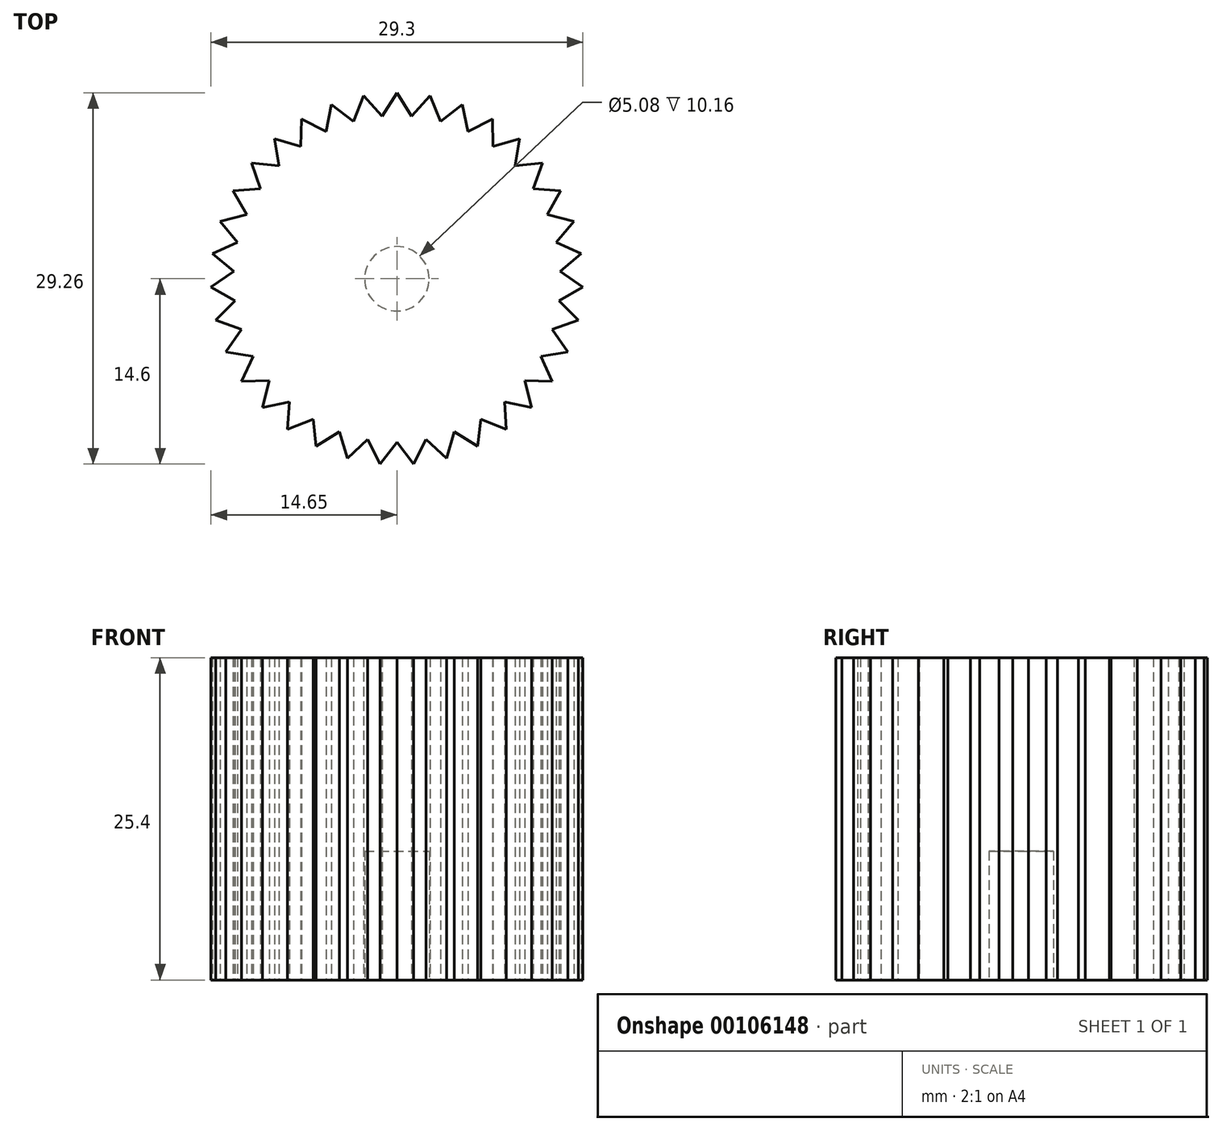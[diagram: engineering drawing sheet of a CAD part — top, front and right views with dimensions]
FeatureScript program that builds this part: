
annotation { "Feature Type Name" : "Feature", "Feature Type Description" : "" }
export const myFeature = defineFeature(function(context is Context, id is Id, definition is map)
    precondition{}
    {
        {
            var Q0;
            Q0=qCreatedBy(makeId("Top.planeOp"),FACE);
            var sketch = newSketch(context, id + "F0", { "sketchPlane" : qUnion([Q0])});
            skCircle(sketch, "E0", {"center": v(0, 0) * mm, "radius": 12.7 * mm});
            skLineSegment(sketch, "E1", {"start": v(-1.27, 12.64) * mm, "end": v(0, 14.66) * mm});
            skLineSegment(sketch, "E2", {"start": v(0, 14.66) * mm, "end": v(1.27, 12.64) * mm});
            skLineSegment(sketch, "E3.1.0", {"start": v(-3.5, 12.2) * mm, "end": v(-2.62, 14.43) * mm});
            skLineSegment(sketch, "E3.1.1", {"start": v(-2.62, 14.43) * mm, "end": v(-1, 12.66) * mm});
            skLineSegment(sketch, "E3.2.0", {"start": v(-5.63, 11.38) * mm, "end": v(-5.15, 13.73) * mm});
            skLineSegment(sketch, "E3.2.1", {"start": v(-5.15, 13.73) * mm, "end": v(-3.25, 12.28) * mm});
            skLineSegment(sketch, "E4.1.3.0", {"start": v(-7.57, 10.2) * mm, "end": v(-7.52, 12.59) * mm});
            skLineSegment(sketch, "E4.3.3.0", {"start": v(-7.52, 12.59) * mm, "end": v(-5.4, 11.5) * mm});
            skLineSegment(sketch, "E4.1.4.0", {"start": v(-9.27, 8.68) * mm, "end": v(-9.65, 11.04) * mm});
            skLineSegment(sketch, "E4.3.4.0", {"start": v(-9.65, 11.04) * mm, "end": v(-7.36, 10.35) * mm});
            skLineSegment(sketch, "E4.1.5.0", {"start": v(-10.67, 6.89) * mm, "end": v(-11.46, 9.14) * mm});
            skLineSegment(sketch, "E4.3.5.0", {"start": v(-11.46, 9.14) * mm, "end": v(-9.09, 8.87) * mm});
            skLineSegment(sketch, "E4.1.6.0", {"start": v(-11.73, 4.87) * mm, "end": v(-12.91, 6.95) * mm});
            skLineSegment(sketch, "E4.3.6.0", {"start": v(-12.91, 6.95) * mm, "end": v(-10.53, 7.1) * mm});
            skLineSegment(sketch, "E4.1.7.0", {"start": v(-12.41, 2.7) * mm, "end": v(-13.94, 4.53) * mm});
            skLineSegment(sketch, "E4.3.7.0", {"start": v(-13.94, 4.53) * mm, "end": v(-11.63, 5.11) * mm});
            skLineSegment(sketch, "E4.1.8.0", {"start": v(-12.7, 0.44) * mm, "end": v(-14.53, 1.97) * mm});
            skLineSegment(sketch, "E4.3.8.0", {"start": v(-14.53, 1.97) * mm, "end": v(-12.35, 2.95) * mm});
            skLineSegment(sketch, "E4.1.9.0", {"start": v(-12.57, -1.84) * mm, "end": v(-14.65, -0.66) * mm});
            skLineSegment(sketch, "E4.3.9.0", {"start": v(-14.65, -0.66) * mm, "end": v(-12.68, 0.7) * mm});
            skLineSegment(sketch, "E4.1.10.0", {"start": v(-12.04, -4.05) * mm, "end": v(-14.3, -3.26) * mm});
            skLineSegment(sketch, "E4.3.10.0", {"start": v(-14.3, -3.26) * mm, "end": v(-12.6, -1.57) * mm});
            skLineSegment(sketch, "E4.1.11.0", {"start": v(-11.12, -6.13) * mm, "end": v(-13.48, -5.76) * mm});
            skLineSegment(sketch, "E4.3.11.0", {"start": v(-13.48, -5.76) * mm, "end": v(-12.12, -3.8) * mm});
            skLineSegment(sketch, "E4.1.12.0", {"start": v(-9.85, -8.02) * mm, "end": v(-12.24, -8.08) * mm});
            skLineSegment(sketch, "E4.3.12.0", {"start": v(-12.24, -8.08) * mm, "end": v(-11.25, -5.9) * mm});
            skLineSegment(sketch, "E4.1.13.0", {"start": v(-8.26, -9.65) * mm, "end": v(-10.6, -10.13) * mm});
            skLineSegment(sketch, "E4.3.13.0", {"start": v(-10.6, -10.13) * mm, "end": v(-10.01, -7.81) * mm});
            skLineSegment(sketch, "E4.1.14.0", {"start": v(-6.4, -10.97) * mm, "end": v(-8.62, -11.86) * mm});
            skLineSegment(sketch, "E4.3.14.0", {"start": v(-8.62, -11.86) * mm, "end": v(-8.45, -9.48) * mm});
            skLineSegment(sketch, "E4.1.15.0", {"start": v(-4.34, -11.94) * mm, "end": v(-6.36, -13.2) * mm});
            skLineSegment(sketch, "E4.3.15.0", {"start": v(-6.36, -13.2) * mm, "end": v(-6.63, -10.83) * mm});
            skLineSegment(sketch, "E4.1.16.0", {"start": v(-2.14, -12.52) * mm, "end": v(-3.9, -14.13) * mm});
            skLineSegment(sketch, "E4.3.16.0", {"start": v(-3.9, -14.13) * mm, "end": v(-4.59, -11.84) * mm});
            skLineSegment(sketch, "E4.1.17.0", {"start": v(0.13, -12.7) * mm, "end": v(-1.31, -14.6) * mm});
            skLineSegment(sketch, "E4.3.17.0", {"start": v(-1.31, -14.6) * mm, "end": v(-2.4, -12.47) * mm});
            skLineSegment(sketch, "E4.1.18.0", {"start": v(2.4, -12.47) * mm, "end": v(1.31, -14.6) * mm});
            skLineSegment(sketch, "E4.3.18.0", {"start": v(1.31, -14.6) * mm, "end": v(-0.13, -12.7) * mm});
            skLineSegment(sketch, "E4.1.19.0", {"start": v(4.59, -11.84) * mm, "end": v(3.9, -14.13) * mm});
            skLineSegment(sketch, "E4.3.19.0", {"start": v(3.9, -14.13) * mm, "end": v(2.14, -12.52) * mm});
            skLineSegment(sketch, "E4.1.20.0", {"start": v(6.63, -10.83) * mm, "end": v(6.36, -13.2) * mm});
            skLineSegment(sketch, "E4.3.20.0", {"start": v(6.36, -13.2) * mm, "end": v(4.34, -11.94) * mm});
            skLineSegment(sketch, "E4.1.21.0", {"start": v(8.45, -9.48) * mm, "end": v(8.62, -11.86) * mm});
            skLineSegment(sketch, "E4.3.21.0", {"start": v(8.62, -11.86) * mm, "end": v(6.4, -10.97) * mm});
            skLineSegment(sketch, "E4.1.22.0", {"start": v(10.01, -7.81) * mm, "end": v(10.6, -10.13) * mm});
            skLineSegment(sketch, "E4.3.22.0", {"start": v(10.6, -10.13) * mm, "end": v(8.26, -9.65) * mm});
            skLineSegment(sketch, "E4.1.23.0", {"start": v(11.25, -5.9) * mm, "end": v(12.24, -8.08) * mm});
            skLineSegment(sketch, "E4.3.23.0", {"start": v(12.24, -8.08) * mm, "end": v(9.85, -8.02) * mm});
            skLineSegment(sketch, "E4.1.24.0", {"start": v(12.12, -3.8) * mm, "end": v(13.48, -5.76) * mm});
            skLineSegment(sketch, "E4.3.24.0", {"start": v(13.48, -5.76) * mm, "end": v(11.12, -6.13) * mm});
            skLineSegment(sketch, "E4.1.25.0", {"start": v(12.6, -1.57) * mm, "end": v(14.3, -3.26) * mm});
            skLineSegment(sketch, "E4.3.25.0", {"start": v(14.3, -3.26) * mm, "end": v(12.04, -4.05) * mm});
            skLineSegment(sketch, "E4.1.26.0", {"start": v(12.68, 0.7) * mm, "end": v(14.65, -0.66) * mm});
            skLineSegment(sketch, "E4.3.26.0", {"start": v(14.65, -0.66) * mm, "end": v(12.57, -1.84) * mm});
            skLineSegment(sketch, "E4.1.27.0", {"start": v(12.35, 2.95) * mm, "end": v(14.53, 1.97) * mm});
            skLineSegment(sketch, "E4.3.27.0", {"start": v(14.53, 1.97) * mm, "end": v(12.7, 0.44) * mm});
            skLineSegment(sketch, "E4.1.28.0", {"start": v(11.63, 5.11) * mm, "end": v(13.94, 4.53) * mm});
            skLineSegment(sketch, "E4.3.28.0", {"start": v(13.94, 4.53) * mm, "end": v(12.41, 2.7) * mm});
            skLineSegment(sketch, "E4.1.29.0", {"start": v(10.53, 7.1) * mm, "end": v(12.91, 6.95) * mm});
            skLineSegment(sketch, "E4.3.29.0", {"start": v(12.91, 6.95) * mm, "end": v(11.73, 4.87) * mm});
            skLineSegment(sketch, "E4.1.30.0", {"start": v(9.09, 8.87) * mm, "end": v(11.46, 9.14) * mm});
            skLineSegment(sketch, "E4.3.30.0", {"start": v(11.46, 9.14) * mm, "end": v(10.67, 6.89) * mm});
            skLineSegment(sketch, "E4.1.31.0", {"start": v(7.36, 10.35) * mm, "end": v(9.65, 11.04) * mm});
            skLineSegment(sketch, "E4.3.31.0", {"start": v(9.65, 11.04) * mm, "end": v(9.27, 8.68) * mm});
            skLineSegment(sketch, "E4.1.32.0", {"start": v(5.4, 11.5) * mm, "end": v(7.52, 12.59) * mm});
            skLineSegment(sketch, "E4.3.32.0", {"start": v(7.52, 12.59) * mm, "end": v(7.57, 10.2) * mm});
            skLineSegment(sketch, "E4.1.33.0", {"start": v(3.25, 12.28) * mm, "end": v(5.15, 13.73) * mm});
            skLineSegment(sketch, "E4.3.33.0", {"start": v(5.15, 13.73) * mm, "end": v(5.63, 11.38) * mm});
            skLineSegment(sketch, "E4.1.34.0", {"start": v(1, 12.66) * mm, "end": v(2.62, 14.43) * mm});
            skLineSegment(sketch, "E4.3.34.0", {"start": v(2.62, 14.43) * mm, "end": v(3.5, 12.2) * mm});
            skSolve(sketch);
        }
        {
            var Q0;
            {var subQ3=sQuery(id+"F0.wireOp",EDGE,"E4.1.12.0");var subQ7=sQuery(id+"F0.wireOp",EDGE,"E0");var subQ8=makeQuery(id+"F0.imprint","INTERSECT",VERTEX,{"derivedFrom":[subQ7,subQ3]});Q0=makeQuery(id+"F0.imprint","IMPRINT",FACE,{"disambiguationData":[TD([[makeQuery(id+"F0.imprint","IMPRINT",EDGE,{"disambiguationData":[TD([[subQ8,-1.0]])],"derivedFrom":subQ7}),-1.0]])]});}
            var Q1;
            {var subQ3=sQuery(id+"F0.wireOp",EDGE,"E4.1.4.0");var subQ7=sQuery(id+"F0.wireOp",EDGE,"E0");var subQ9=makeQuery(id+"F0.imprint","INTERSECT",VERTEX,{"derivedFrom":[subQ7,subQ3]});Q1=makeQuery(id+"F0.imprint","IMPRINT",FACE,{"disambiguationData":[TD([[makeQuery(id+"F0.imprint","IMPRINT",EDGE,{"disambiguationData":[TD([[subQ9,-1.0]])],"derivedFrom":subQ7}),-1.0]])]});}
            var Q2;
            {var subQ5=sQuery(id+"F0.wireOp",EDGE,"E4.1.31.0");var subQ6=sQuery(id+"F0.wireOp",EDGE,"E0");var subQ7=makeQuery(id+"F0.imprint","INTERSECT",VERTEX,{"derivedFrom":[subQ6,subQ5]});Q2=makeQuery(id+"F0.imprint","IMPRINT",FACE,{"disambiguationData":[TD([[makeQuery(id+"F0.imprint","IMPRINT",EDGE,{"disambiguationData":[TD([[subQ7,-1.0]])],"derivedFrom":subQ6}),-1.0]])]});}
            var Q3;
            {var subQ3=sQuery(id+"F0.wireOp",EDGE,"E4.1.20.0");var subQ7=sQuery(id+"F0.wireOp",EDGE,"E0");var subQ8=makeQuery(id+"F0.imprint","INTERSECT",VERTEX,{"derivedFrom":[subQ7,subQ3]});Q3=makeQuery(id+"F0.imprint","IMPRINT",FACE,{"disambiguationData":[TD([[makeQuery(id+"F0.imprint","IMPRINT",EDGE,{"disambiguationData":[TD([[subQ8,-1.0]])],"derivedFrom":subQ7}),-1.0]])]});}
            var Q4;
            {var subQ3=sQuery(id+"F0.wireOp",EDGE,"E4.1.30.0");var subQ7=sQuery(id+"F0.wireOp",EDGE,"E0");var subQ8=makeQuery(id+"F0.imprint","INTERSECT",VERTEX,{"derivedFrom":[subQ7,subQ3]});Q4=makeQuery(id+"F0.imprint","IMPRINT",FACE,{"disambiguationData":[TD([[makeQuery(id+"F0.imprint","IMPRINT",EDGE,{"disambiguationData":[TD([[subQ8,-1.0]])],"derivedFrom":subQ7}),-1.0]])]});}
            var Q5;
            {var subQ5=sQuery(id+"F0.wireOp",EDGE,"E4.1.29.0");var subQ6=sQuery(id+"F0.wireOp",EDGE,"E0");var subQ7=makeQuery(id+"F0.imprint","INTERSECT",VERTEX,{"derivedFrom":[subQ6,subQ5]});Q5=makeQuery(id+"F0.imprint","IMPRINT",FACE,{"disambiguationData":[TD([[makeQuery(id+"F0.imprint","IMPRINT",EDGE,{"disambiguationData":[TD([[subQ7,-1.0]])],"derivedFrom":subQ6}),-1.0]])]});}
            var Q6;
            {var subQ3=sQuery(id+"F0.wireOp",EDGE,"E4.1.28.0");var subQ5=sQuery(id+"F0.wireOp",EDGE,"E0");var subQ6=makeQuery(id+"F0.imprint","INTERSECT",VERTEX,{"derivedFrom":[subQ5,subQ3]});Q6=makeQuery(id+"F0.imprint","IMPRINT",FACE,{"disambiguationData":[TD([[makeQuery(id+"F0.imprint","IMPRINT",EDGE,{"disambiguationData":[TD([[subQ6,-1.0]])],"derivedFrom":subQ5}),-1.0]])]});}
            var Q7;
            {var subQ3=sQuery(id+"F0.wireOp",EDGE,"E4.1.27.0");var subQ7=sQuery(id+"F0.wireOp",EDGE,"E0");var subQ8=makeQuery(id+"F0.imprint","INTERSECT",VERTEX,{"derivedFrom":[subQ7,subQ3]});Q7=makeQuery(id+"F0.imprint","IMPRINT",FACE,{"disambiguationData":[TD([[makeQuery(id+"F0.imprint","IMPRINT",EDGE,{"disambiguationData":[TD([[subQ8,-1.0]])],"derivedFrom":subQ7}),-1.0]])]});}
            var Q8;
            {var subQ3=sQuery(id+"F0.wireOp",EDGE,"E4.1.19.0");var subQ5=sQuery(id+"F0.wireOp",EDGE,"E0");var subQ6=makeQuery(id+"F0.imprint","INTERSECT",VERTEX,{"derivedFrom":[subQ5,subQ3]});Q8=makeQuery(id+"F0.imprint","IMPRINT",FACE,{"disambiguationData":[TD([[makeQuery(id+"F0.imprint","IMPRINT",EDGE,{"disambiguationData":[TD([[subQ6,-1.0]])],"derivedFrom":subQ5}),-1.0]])]});}
            var Q9;
            {var subQ3=sQuery(id+"F0.wireOp",EDGE,"E4.1.11.0");var subQ5=sQuery(id+"F0.wireOp",EDGE,"E0");var subQ6=makeQuery(id+"F0.imprint","INTERSECT",VERTEX,{"derivedFrom":[subQ5,subQ3]});Q9=makeQuery(id+"F0.imprint","IMPRINT",FACE,{"disambiguationData":[TD([[makeQuery(id+"F0.imprint","IMPRINT",EDGE,{"disambiguationData":[TD([[subQ6,-1.0]])],"derivedFrom":subQ5}),-1.0]])]});}
            var Q10;
            {var subQ3=sQuery(id+"F0.wireOp",EDGE,"E4.1.6.0");var subQ5=sQuery(id+"F0.wireOp",EDGE,"E0");var subQ6=makeQuery(id+"F0.imprint","INTERSECT",VERTEX,{"derivedFrom":[subQ5,subQ3]});Q10=makeQuery(id+"F0.imprint","IMPRINT",FACE,{"disambiguationData":[TD([[makeQuery(id+"F0.imprint","IMPRINT",EDGE,{"disambiguationData":[TD([[subQ6,-1.0]])],"derivedFrom":subQ5}),-1.0]])]});}
            var Q11;
            {var subQ3=sQuery(id+"F0.wireOp",EDGE,"E4.1.3.0");var subQ7=sQuery(id+"F0.wireOp",EDGE,"E0");var subQ8=makeQuery(id+"F0.imprint","INTERSECT",VERTEX,{"derivedFrom":[subQ7,subQ3]});Q11=makeQuery(id+"F0.imprint","IMPRINT",FACE,{"disambiguationData":[TD([[makeQuery(id+"F0.imprint","IMPRINT",EDGE,{"disambiguationData":[TD([[subQ8,-1.0]])],"derivedFrom":subQ7}),-1.0]])]});}
            var Q12;
            {var subQ3=sQuery(id+"F0.wireOp",EDGE,"E4.1.22.0");var subQ7=sQuery(id+"F0.wireOp",EDGE,"E0");var subQ8=makeQuery(id+"F0.imprint","INTERSECT",VERTEX,{"derivedFrom":[subQ7,subQ3]});Q12=makeQuery(id+"F0.imprint","IMPRINT",FACE,{"disambiguationData":[TD([[makeQuery(id+"F0.imprint","IMPRINT",EDGE,{"disambiguationData":[TD([[subQ8,-1.0]])],"derivedFrom":subQ7}),-1.0]])]});}
            var Q13;
            {var subQ3=sQuery(id+"F0.wireOp",EDGE,"E4.1.14.0");var subQ7=sQuery(id+"F0.wireOp",EDGE,"E0");var subQ8=makeQuery(id+"F0.imprint","INTERSECT",VERTEX,{"derivedFrom":[subQ7,subQ3]});Q13=makeQuery(id+"F0.imprint","IMPRINT",FACE,{"disambiguationData":[TD([[makeQuery(id+"F0.imprint","IMPRINT",EDGE,{"disambiguationData":[TD([[subQ8,-1.0]])],"derivedFrom":subQ7}),-1.0]])]});}
            var Q14;
            {var subQ3=sQuery(id+"F0.wireOp",EDGE,"E4.1.26.0");var subQ5=sQuery(id+"F0.wireOp",EDGE,"E0");var subQ6=makeQuery(id+"F0.imprint","INTERSECT",VERTEX,{"derivedFrom":[subQ5,subQ3]});Q14=makeQuery(id+"F0.imprint","IMPRINT",FACE,{"disambiguationData":[TD([[makeQuery(id+"F0.imprint","IMPRINT",EDGE,{"disambiguationData":[TD([[subQ6,-1.0]])],"derivedFrom":subQ5}),-1.0]])]});}
            var Q15;
            {var subQ3=sQuery(id+"F0.wireOp",EDGE,"E4.1.32.0");var subQ7=sQuery(id+"F0.wireOp",EDGE,"E0");var subQ8=makeQuery(id+"F0.imprint","INTERSECT",VERTEX,{"derivedFrom":[subQ7,subQ3]});Q15=makeQuery(id+"F0.imprint","IMPRINT",FACE,{"disambiguationData":[TD([[makeQuery(id+"F0.imprint","IMPRINT",EDGE,{"disambiguationData":[TD([[subQ8,-1.0]])],"derivedFrom":subQ7}),-1.0]])]});}
            var Q16;
            {var subQ3=sQuery(id+"F0.wireOp",EDGE,"E2");var subQ6=sQuery(id+"F0.wireOp",EDGE,"E0");var subQ9=makeQuery(id+"F0.imprint","INTERSECT",VERTEX,{"derivedFrom":[subQ6,subQ3]});Q16=makeQuery(id+"F0.imprint","IMPRINT",FACE,{"disambiguationData":[TD([[makeQuery(id+"F0.imprint","IMPRINT",EDGE,{"disambiguationData":[TD([[subQ9,1.0]])],"derivedFrom":subQ6}),-1.0]])]});}
            var Q17;
            {var subQ3=sQuery(id+"F0.wireOp",EDGE,"E4.1.5.0");var subQ7=sQuery(id+"F0.wireOp",EDGE,"E0");var subQ8=makeQuery(id+"F0.imprint","INTERSECT",VERTEX,{"derivedFrom":[subQ7,subQ3]});Q17=makeQuery(id+"F0.imprint","IMPRINT",FACE,{"disambiguationData":[TD([[makeQuery(id+"F0.imprint","IMPRINT",EDGE,{"disambiguationData":[TD([[subQ8,-1.0]])],"derivedFrom":subQ7}),-1.0]])]});}
            var Q18;
            {var subQ0=sQuery(id+"F0.wireOp",EDGE,"E0");var subQ35=makeQuery(id+"F0.imprint","INTERSECT",VERTEX,{"derivedFrom":[subQ0,sQuery(id+"F0.wireOp",EDGE,"E4.1.26.0")]});Q18=makeQuery(id+"F0.imprint","IMPRINT",FACE,{"disambiguationData":[TD([[makeQuery(id+"F0.imprint","IMPRINT",EDGE,{"disambiguationData":[TD([[subQ35,1.0]])],"derivedFrom":subQ0}),1.0]])]});}
            var Q19;
            {var subQ3=sQuery(id+"F0.wireOp",EDGE,"E4.1.13.0");var subQ7=sQuery(id+"F0.wireOp",EDGE,"E0");var subQ8=makeQuery(id+"F0.imprint","INTERSECT",VERTEX,{"derivedFrom":[subQ7,subQ3]});Q19=makeQuery(id+"F0.imprint","IMPRINT",FACE,{"disambiguationData":[TD([[makeQuery(id+"F0.imprint","IMPRINT",EDGE,{"disambiguationData":[TD([[subQ8,-1.0]])],"derivedFrom":subQ7}),-1.0]])]});}
            var Q20;
            {var subQ0=sQuery(id+"F0.wireOp",EDGE,"E3.1.1");var subQ1=sQuery(id+"F0.wireOp",EDGE,"E0");var subQ2=makeQuery(id+"F0.imprint","INTERSECT",VERTEX,{"derivedFrom":[subQ1,subQ0]});Q20=makeQuery(id+"F0.imprint","IMPRINT",FACE,{"disambiguationData":[TD([[makeQuery(id+"F0.imprint","IMPRINT",EDGE,{"disambiguationData":[TD([[subQ2,1.0]])],"derivedFrom":subQ1}),-1.0]])]});}
            var Q21;
            {var subQ3=sQuery(id+"F0.wireOp",EDGE,"E4.1.23.0");var subQ7=sQuery(id+"F0.wireOp",EDGE,"E0");var subQ9=makeQuery(id+"F0.imprint","INTERSECT",VERTEX,{"derivedFrom":[subQ7,subQ3]});Q21=makeQuery(id+"F0.imprint","IMPRINT",FACE,{"disambiguationData":[TD([[makeQuery(id+"F0.imprint","IMPRINT",EDGE,{"disambiguationData":[TD([[subQ9,-1.0]])],"derivedFrom":subQ7}),-1.0]])]});}
            var Q22;
            {var subQ3=sQuery(id+"F0.wireOp",EDGE,"E4.1.15.0");var subQ5=sQuery(id+"F0.wireOp",EDGE,"E0");var subQ6=makeQuery(id+"F0.imprint","INTERSECT",VERTEX,{"derivedFrom":[subQ5,subQ3]});Q22=makeQuery(id+"F0.imprint","IMPRINT",FACE,{"disambiguationData":[TD([[makeQuery(id+"F0.imprint","IMPRINT",EDGE,{"disambiguationData":[TD([[subQ6,-1.0]])],"derivedFrom":subQ5}),-1.0]])]});}
            var Q23;
            {var subQ3=sQuery(id+"F0.wireOp",EDGE,"E4.1.7.0");var subQ5=sQuery(id+"F0.wireOp",EDGE,"E0");var subQ6=makeQuery(id+"F0.imprint","INTERSECT",VERTEX,{"derivedFrom":[subQ5,subQ3]});Q23=makeQuery(id+"F0.imprint","IMPRINT",FACE,{"disambiguationData":[TD([[makeQuery(id+"F0.imprint","IMPRINT",EDGE,{"disambiguationData":[TD([[subQ6,-1.0]])],"derivedFrom":subQ5}),-1.0]])]});}
            var Q24;
            {var subQ3=sQuery(id+"F0.wireOp",EDGE,"E4.1.21.0");var subQ7=sQuery(id+"F0.wireOp",EDGE,"E0");var subQ9=makeQuery(id+"F0.imprint","INTERSECT",VERTEX,{"derivedFrom":[subQ7,subQ3]});Q24=makeQuery(id+"F0.imprint","IMPRINT",FACE,{"disambiguationData":[TD([[makeQuery(id+"F0.imprint","IMPRINT",EDGE,{"disambiguationData":[TD([[subQ9,-1.0]])],"derivedFrom":subQ7}),-1.0]])]});}
            var Q25;
            {var subQ5=sQuery(id+"F0.wireOp",EDGE,"E4.1.9.0");var subQ6=sQuery(id+"F0.wireOp",EDGE,"E0");var subQ7=makeQuery(id+"F0.imprint","INTERSECT",VERTEX,{"derivedFrom":[subQ6,subQ5]});Q25=makeQuery(id+"F0.imprint","IMPRINT",FACE,{"disambiguationData":[TD([[makeQuery(id+"F0.imprint","IMPRINT",EDGE,{"disambiguationData":[TD([[subQ7,-1.0]])],"derivedFrom":subQ6}),-1.0]])]});}
            var Q26;
            {var subQ5=sQuery(id+"F0.wireOp",EDGE,"E4.1.17.0");var subQ6=sQuery(id+"F0.wireOp",EDGE,"E0");var subQ7=makeQuery(id+"F0.imprint","INTERSECT",VERTEX,{"derivedFrom":[subQ6,subQ5]});Q26=makeQuery(id+"F0.imprint","IMPRINT",FACE,{"disambiguationData":[TD([[makeQuery(id+"F0.imprint","IMPRINT",EDGE,{"disambiguationData":[TD([[subQ7,-1.0]])],"derivedFrom":subQ6}),-1.0]])]});}
            var Q27;
            {var subQ5=sQuery(id+"F0.wireOp",EDGE,"E4.1.25.0");var subQ6=sQuery(id+"F0.wireOp",EDGE,"E0");var subQ7=makeQuery(id+"F0.imprint","INTERSECT",VERTEX,{"derivedFrom":[subQ6,subQ5]});Q27=makeQuery(id+"F0.imprint","IMPRINT",FACE,{"disambiguationData":[TD([[makeQuery(id+"F0.imprint","IMPRINT",EDGE,{"disambiguationData":[TD([[subQ7,-1.0]])],"derivedFrom":subQ6}),-1.0]])]});}
            var Q28;
            {var subQ5=sQuery(id+"F0.wireOp",EDGE,"E3.1.0");var subQ6=sQuery(id+"F0.wireOp",EDGE,"E0");var subQ7=makeQuery(id+"F0.imprint","INTERSECT",VERTEX,{"derivedFrom":[subQ6,subQ5]});Q28=makeQuery(id+"F0.imprint","IMPRINT",FACE,{"disambiguationData":[TD([[makeQuery(id+"F0.imprint","IMPRINT",EDGE,{"disambiguationData":[TD([[subQ7,-1.0]])],"derivedFrom":subQ6}),-1.0]])]});}
            var Q29;
            {var subQ3=sQuery(id+"F0.wireOp",EDGE,"E4.1.16.0");var subQ7=sQuery(id+"F0.wireOp",EDGE,"E0");var subQ8=makeQuery(id+"F0.imprint","INTERSECT",VERTEX,{"derivedFrom":[subQ7,subQ3]});Q29=makeQuery(id+"F0.imprint","IMPRINT",FACE,{"disambiguationData":[TD([[makeQuery(id+"F0.imprint","IMPRINT",EDGE,{"disambiguationData":[TD([[subQ8,-1.0]])],"derivedFrom":subQ7}),-1.0]])]});}
            var Q30;
            {var subQ3=sQuery(id+"F0.wireOp",EDGE,"E4.1.24.0");var subQ5=sQuery(id+"F0.wireOp",EDGE,"E0");var subQ6=makeQuery(id+"F0.imprint","INTERSECT",VERTEX,{"derivedFrom":[subQ5,subQ3]});Q30=makeQuery(id+"F0.imprint","IMPRINT",FACE,{"disambiguationData":[TD([[makeQuery(id+"F0.imprint","IMPRINT",EDGE,{"disambiguationData":[TD([[subQ6,-1.0]])],"derivedFrom":subQ5}),-1.0]])]});}
            var Q31;
            {var subQ3=sQuery(id+"F0.wireOp",EDGE,"E4.1.8.0");var subQ7=sQuery(id+"F0.wireOp",EDGE,"E0");var subQ8=makeQuery(id+"F0.imprint","INTERSECT",VERTEX,{"derivedFrom":[subQ7,subQ3]});Q31=makeQuery(id+"F0.imprint","IMPRINT",FACE,{"disambiguationData":[TD([[makeQuery(id+"F0.imprint","IMPRINT",EDGE,{"disambiguationData":[TD([[subQ8,-1.0]])],"derivedFrom":subQ7}),-1.0]])]});}
            var Q32;
            {var subQ3=sQuery(id+"F0.wireOp",EDGE,"E1");var subQ7=sQuery(id+"F0.wireOp",EDGE,"E0");var subQ8=makeQuery(id+"F0.imprint","INTERSECT",VERTEX,{"derivedFrom":[subQ7,subQ3]});Q32=makeQuery(id+"F0.imprint","IMPRINT",FACE,{"disambiguationData":[TD([[makeQuery(id+"F0.imprint","IMPRINT",EDGE,{"disambiguationData":[TD([[subQ8,-1.0]])],"derivedFrom":subQ7}),-1.0]])]});}
            var Q33;
            {var subQ0=sQuery(id+"F0.wireOp",EDGE,"E3.2.0");var subQ1=sQuery(id+"F0.wireOp",EDGE,"E0");var subQ2=makeQuery(id+"F0.imprint","INTERSECT",VERTEX,{"derivedFrom":[subQ1,subQ0]});Q33=makeQuery(id+"F0.imprint","IMPRINT",FACE,{"disambiguationData":[TD([[makeQuery(id+"F0.imprint","IMPRINT",EDGE,{"disambiguationData":[TD([[subQ2,-1.0]])],"derivedFrom":subQ1}),-1.0]])]});}
            var Q34;
            {var subQ0=sQuery(id+"F0.wireOp",EDGE,"E4.1.10.0");var subQ1=sQuery(id+"F0.wireOp",EDGE,"E0");var subQ2=makeQuery(id+"F0.imprint","INTERSECT",VERTEX,{"derivedFrom":[subQ1,subQ0]});Q34=makeQuery(id+"F0.imprint","IMPRINT",FACE,{"disambiguationData":[TD([[makeQuery(id+"F0.imprint","IMPRINT",EDGE,{"disambiguationData":[TD([[subQ2,-1.0]])],"derivedFrom":subQ1}),-1.0]])]});}
            var Q35;
            {var subQ3=sQuery(id+"F0.wireOp",EDGE,"E4.1.18.0");var subQ7=sQuery(id+"F0.wireOp",EDGE,"E0");var subQ8=makeQuery(id+"F0.imprint","INTERSECT",VERTEX,{"derivedFrom":[subQ7,subQ3]});Q35=makeQuery(id+"F0.imprint","IMPRINT",FACE,{"disambiguationData":[TD([[makeQuery(id+"F0.imprint","IMPRINT",EDGE,{"disambiguationData":[TD([[subQ8,-1.0]])],"derivedFrom":subQ7}),-1.0]])]});}
            var Q36;
            {var subQ0=sQuery(id+"F0.wireOp",EDGE,"E4.1.32.0");var subQ1=sQuery(id+"F0.wireOp",EDGE,"E0");var subQ2=makeQuery(id+"F0.imprint","INTERSECT",VERTEX,{"derivedFrom":[subQ1,subQ0]});Q36=makeQuery(id+"F0.imprint","IMPRINT",FACE,{"disambiguationData":[TD([[makeQuery(id+"F0.imprint","IMPRINT",EDGE,{"disambiguationData":[TD([[subQ2,1.0]])],"derivedFrom":subQ1}),-1.0]])]});}
            var Q37;
            {var subQ0=sQuery(id+"F0.wireOp",EDGE,"E4.1.19.0");var subQ1=sQuery(id+"F0.wireOp",EDGE,"E0");var subQ2=makeQuery(id+"F0.imprint","INTERSECT",VERTEX,{"derivedFrom":[subQ1,subQ0]});Q37=makeQuery(id+"F0.imprint","IMPRINT",FACE,{"disambiguationData":[TD([[makeQuery(id+"F0.imprint","IMPRINT",EDGE,{"disambiguationData":[TD([[subQ2,1.0]])],"derivedFrom":subQ1}),-1.0]])]});}
            var Q38;
            {var subQ0=sQuery(id+"F0.wireOp",EDGE,"E4.1.31.0");var subQ1=sQuery(id+"F0.wireOp",EDGE,"E0");var subQ2=makeQuery(id+"F0.imprint","INTERSECT",VERTEX,{"derivedFrom":[subQ1,subQ0]});Q38=makeQuery(id+"F0.imprint","IMPRINT",FACE,{"disambiguationData":[TD([[makeQuery(id+"F0.imprint","IMPRINT",EDGE,{"disambiguationData":[TD([[subQ2,1.0]])],"derivedFrom":subQ1}),-1.0]])]});}
            var Q39;
            {var subQ0=sQuery(id+"F0.wireOp",EDGE,"E4.1.15.0");var subQ1=sQuery(id+"F0.wireOp",EDGE,"E0");var subQ2=makeQuery(id+"F0.imprint","INTERSECT",VERTEX,{"derivedFrom":[subQ1,subQ0]});Q39=makeQuery(id+"F0.imprint","IMPRINT",FACE,{"disambiguationData":[TD([[makeQuery(id+"F0.imprint","IMPRINT",EDGE,{"disambiguationData":[TD([[subQ2,1.0]])],"derivedFrom":subQ1}),-1.0]])]});}
            var Q40;
            {var subQ0=sQuery(id+"F0.wireOp",EDGE,"E4.1.29.0");var subQ1=sQuery(id+"F0.wireOp",EDGE,"E0");var subQ2=makeQuery(id+"F0.imprint","INTERSECT",VERTEX,{"derivedFrom":[subQ1,subQ0]});Q40=makeQuery(id+"F0.imprint","IMPRINT",FACE,{"disambiguationData":[TD([[makeQuery(id+"F0.imprint","IMPRINT",EDGE,{"disambiguationData":[TD([[subQ2,1.0]])],"derivedFrom":subQ1}),-1.0]])]});}
            var Q41;
            {var subQ0=sQuery(id+"F0.wireOp",EDGE,"E4.1.30.0");var subQ1=sQuery(id+"F0.wireOp",EDGE,"E0");var subQ2=makeQuery(id+"F0.imprint","INTERSECT",VERTEX,{"derivedFrom":[subQ1,subQ0]});Q41=makeQuery(id+"F0.imprint","IMPRINT",FACE,{"disambiguationData":[TD([[makeQuery(id+"F0.imprint","IMPRINT",EDGE,{"disambiguationData":[TD([[subQ2,1.0]])],"derivedFrom":subQ1}),-1.0]])]});}
            var Q42;
            {var subQ0=sQuery(id+"F0.wireOp",EDGE,"E4.1.23.0");var subQ1=sQuery(id+"F0.wireOp",EDGE,"E0");var subQ2=makeQuery(id+"F0.imprint","INTERSECT",VERTEX,{"derivedFrom":[subQ1,subQ0]});Q42=makeQuery(id+"F0.imprint","IMPRINT",FACE,{"disambiguationData":[TD([[makeQuery(id+"F0.imprint","IMPRINT",EDGE,{"disambiguationData":[TD([[subQ2,1.0]])],"derivedFrom":subQ1}),-1.0]])]});}
            var Q43;
            {var subQ0=sQuery(id+"F0.wireOp",EDGE,"E4.1.28.0");var subQ1=sQuery(id+"F0.wireOp",EDGE,"E0");var subQ2=makeQuery(id+"F0.imprint","INTERSECT",VERTEX,{"derivedFrom":[subQ1,subQ0]});Q43=makeQuery(id+"F0.imprint","IMPRINT",FACE,{"disambiguationData":[TD([[makeQuery(id+"F0.imprint","IMPRINT",EDGE,{"disambiguationData":[TD([[subQ2,1.0]])],"derivedFrom":subQ1}),-1.0]])]});}
            var Q44;
            {var subQ0=sQuery(id+"F0.wireOp",EDGE,"E4.1.7.0");var subQ1=sQuery(id+"F0.wireOp",EDGE,"E0");var subQ2=makeQuery(id+"F0.imprint","INTERSECT",VERTEX,{"derivedFrom":[subQ1,subQ0]});Q44=makeQuery(id+"F0.imprint","IMPRINT",FACE,{"disambiguationData":[TD([[makeQuery(id+"F0.imprint","IMPRINT",EDGE,{"disambiguationData":[TD([[subQ2,1.0]])],"derivedFrom":subQ1}),-1.0]])]});}
            var Q45;
            {var subQ0=sQuery(id+"F0.wireOp",EDGE,"E4.1.11.0");var subQ1=sQuery(id+"F0.wireOp",EDGE,"E0");var subQ2=makeQuery(id+"F0.imprint","INTERSECT",VERTEX,{"derivedFrom":[subQ1,subQ0]});Q45=makeQuery(id+"F0.imprint","IMPRINT",FACE,{"disambiguationData":[TD([[makeQuery(id+"F0.imprint","IMPRINT",EDGE,{"disambiguationData":[TD([[subQ2,1.0]])],"derivedFrom":subQ1}),-1.0]])]});}
            var Q46;
            {var subQ0=sQuery(id+"F0.wireOp",EDGE,"E4.1.3.0");var subQ1=sQuery(id+"F0.wireOp",EDGE,"E0");var subQ2=makeQuery(id+"F0.imprint","INTERSECT",VERTEX,{"derivedFrom":[subQ1,subQ0]});Q46=makeQuery(id+"F0.imprint","IMPRINT",FACE,{"disambiguationData":[TD([[makeQuery(id+"F0.imprint","IMPRINT",EDGE,{"disambiguationData":[TD([[subQ2,1.0]])],"derivedFrom":subQ1}),-1.0]])]});}
            var Q47;
            {var subQ0=sQuery(id+"F0.wireOp",EDGE,"E4.1.27.0");var subQ1=sQuery(id+"F0.wireOp",EDGE,"E0");var subQ2=makeQuery(id+"F0.imprint","INTERSECT",VERTEX,{"derivedFrom":[subQ1,subQ0]});Q47=makeQuery(id+"F0.imprint","IMPRINT",FACE,{"disambiguationData":[TD([[makeQuery(id+"F0.imprint","IMPRINT",EDGE,{"disambiguationData":[TD([[subQ2,1.0]])],"derivedFrom":subQ1}),-1.0]])]});}
            var Q48;
            {var subQ0=sQuery(id+"F0.wireOp",EDGE,"E4.1.26.0");var subQ1=sQuery(id+"F0.wireOp",EDGE,"E0");var subQ2=makeQuery(id+"F0.imprint","INTERSECT",VERTEX,{"derivedFrom":[subQ1,subQ0]});Q48=makeQuery(id+"F0.imprint","IMPRINT",FACE,{"disambiguationData":[TD([[makeQuery(id+"F0.imprint","IMPRINT",EDGE,{"disambiguationData":[TD([[subQ2,1.0]])],"derivedFrom":subQ1}),-1.0]])]});}
            var Q49;
            {var subQ0=sQuery(id+"F0.wireOp",EDGE,"E4.1.33.0");var subQ1=sQuery(id+"F0.wireOp",EDGE,"E0");var subQ2=makeQuery(id+"F0.imprint","INTERSECT",VERTEX,{"derivedFrom":[subQ1,subQ0]});Q49=makeQuery(id+"F0.imprint","IMPRINT",FACE,{"disambiguationData":[TD([[makeQuery(id+"F0.imprint","IMPRINT",EDGE,{"disambiguationData":[TD([[subQ2,1.0]])],"derivedFrom":subQ1}),-1.0]])]});}
            var Q50;
            {var subQ0=sQuery(id+"F0.wireOp",EDGE,"E4.1.22.0");var subQ1=sQuery(id+"F0.wireOp",EDGE,"E0");var subQ2=makeQuery(id+"F0.imprint","INTERSECT",VERTEX,{"derivedFrom":[subQ1,subQ0]});Q50=makeQuery(id+"F0.imprint","IMPRINT",FACE,{"disambiguationData":[TD([[makeQuery(id+"F0.imprint","IMPRINT",EDGE,{"disambiguationData":[TD([[subQ2,1.0]])],"derivedFrom":subQ1}),-1.0]])]});}
            var Q51;
            {var subQ0=sQuery(id+"F0.wireOp",EDGE,"E3.2.0");var subQ1=sQuery(id+"F0.wireOp",EDGE,"E0");var subQ2=makeQuery(id+"F0.imprint","INTERSECT",VERTEX,{"derivedFrom":[subQ1,subQ0]});Q51=makeQuery(id+"F0.imprint","IMPRINT",FACE,{"disambiguationData":[TD([[makeQuery(id+"F0.imprint","IMPRINT",EDGE,{"disambiguationData":[TD([[subQ2,1.0]])],"derivedFrom":subQ1}),-1.0]])]});}
            var Q52;
            {var subQ0=sQuery(id+"F0.wireOp",EDGE,"E4.1.10.0");var subQ1=sQuery(id+"F0.wireOp",EDGE,"E0");var subQ2=makeQuery(id+"F0.imprint","INTERSECT",VERTEX,{"derivedFrom":[subQ1,subQ0]});Q52=makeQuery(id+"F0.imprint","IMPRINT",FACE,{"disambiguationData":[TD([[makeQuery(id+"F0.imprint","IMPRINT",EDGE,{"disambiguationData":[TD([[subQ2,1.0]])],"derivedFrom":subQ1}),-1.0]])]});}
            var Q53;
            {var subQ0=sQuery(id+"F0.wireOp",EDGE,"E4.1.18.0");var subQ1=sQuery(id+"F0.wireOp",EDGE,"E0");var subQ2=makeQuery(id+"F0.imprint","INTERSECT",VERTEX,{"derivedFrom":[subQ1,subQ0]});Q53=makeQuery(id+"F0.imprint","IMPRINT",FACE,{"disambiguationData":[TD([[makeQuery(id+"F0.imprint","IMPRINT",EDGE,{"disambiguationData":[TD([[subQ2,1.0]])],"derivedFrom":subQ1}),-1.0]])]});}
            var Q54;
            {var subQ0=sQuery(id+"F0.wireOp",EDGE,"E4.1.14.0");var subQ1=sQuery(id+"F0.wireOp",EDGE,"E0");var subQ2=makeQuery(id+"F0.imprint","INTERSECT",VERTEX,{"derivedFrom":[subQ1,subQ0]});Q54=makeQuery(id+"F0.imprint","IMPRINT",FACE,{"disambiguationData":[TD([[makeQuery(id+"F0.imprint","IMPRINT",EDGE,{"disambiguationData":[TD([[subQ2,1.0]])],"derivedFrom":subQ1}),-1.0]])]});}
            var Q55;
            {var subQ0=sQuery(id+"F0.wireOp",EDGE,"E4.1.6.0");var subQ1=sQuery(id+"F0.wireOp",EDGE,"E0");var subQ2=makeQuery(id+"F0.imprint","INTERSECT",VERTEX,{"derivedFrom":[subQ1,subQ0]});Q55=makeQuery(id+"F0.imprint","IMPRINT",FACE,{"disambiguationData":[TD([[makeQuery(id+"F0.imprint","IMPRINT",EDGE,{"disambiguationData":[TD([[subQ2,1.0]])],"derivedFrom":subQ1}),-1.0]])]});}
            var Q56;
            {var subQ0=sQuery(id+"F0.wireOp",EDGE,"E4.1.20.0");var subQ1=sQuery(id+"F0.wireOp",EDGE,"E0");var subQ2=makeQuery(id+"F0.imprint","INTERSECT",VERTEX,{"derivedFrom":[subQ1,subQ0]});Q56=makeQuery(id+"F0.imprint","IMPRINT",FACE,{"disambiguationData":[TD([[makeQuery(id+"F0.imprint","IMPRINT",EDGE,{"disambiguationData":[TD([[subQ2,1.0]])],"derivedFrom":subQ1}),-1.0]])]});}
            var Q57;
            {var subQ0=sQuery(id+"F0.wireOp",EDGE,"E4.1.4.0");var subQ1=sQuery(id+"F0.wireOp",EDGE,"E0");var subQ2=makeQuery(id+"F0.imprint","INTERSECT",VERTEX,{"derivedFrom":[subQ1,subQ0]});Q57=makeQuery(id+"F0.imprint","IMPRINT",FACE,{"disambiguationData":[TD([[makeQuery(id+"F0.imprint","IMPRINT",EDGE,{"disambiguationData":[TD([[subQ2,1.0]])],"derivedFrom":subQ1}),-1.0]])]});}
            var Q58;
            {var subQ0=sQuery(id+"F0.wireOp",EDGE,"E4.1.12.0");var subQ1=sQuery(id+"F0.wireOp",EDGE,"E0");var subQ2=makeQuery(id+"F0.imprint","INTERSECT",VERTEX,{"derivedFrom":[subQ1,subQ0]});Q58=makeQuery(id+"F0.imprint","IMPRINT",FACE,{"disambiguationData":[TD([[makeQuery(id+"F0.imprint","IMPRINT",EDGE,{"disambiguationData":[TD([[subQ2,1.0]])],"derivedFrom":subQ1}),-1.0]])]});}
            var Q59;
            {var subQ0=sQuery(id+"F0.wireOp",EDGE,"E4.1.13.0");var subQ1=sQuery(id+"F0.wireOp",EDGE,"E0");var subQ2=makeQuery(id+"F0.imprint","INTERSECT",VERTEX,{"derivedFrom":[subQ1,subQ0]});Q59=makeQuery(id+"F0.imprint","IMPRINT",FACE,{"disambiguationData":[TD([[makeQuery(id+"F0.imprint","IMPRINT",EDGE,{"disambiguationData":[TD([[subQ2,1.0]])],"derivedFrom":subQ1}),-1.0]])]});}
            var Q60;
            {var subQ0=sQuery(id+"F0.wireOp",EDGE,"E4.1.5.0");var subQ1=sQuery(id+"F0.wireOp",EDGE,"E0");var subQ2=makeQuery(id+"F0.imprint","INTERSECT",VERTEX,{"derivedFrom":[subQ1,subQ0]});Q60=makeQuery(id+"F0.imprint","IMPRINT",FACE,{"disambiguationData":[TD([[makeQuery(id+"F0.imprint","IMPRINT",EDGE,{"disambiguationData":[TD([[subQ2,1.0]])],"derivedFrom":subQ1}),-1.0]])]});}
            var Q61;
            {var subQ0=sQuery(id+"F0.wireOp",EDGE,"E1");var subQ1=sQuery(id+"F0.wireOp",EDGE,"E0");var subQ2=makeQuery(id+"F0.imprint","INTERSECT",VERTEX,{"derivedFrom":[subQ1,subQ0]});Q61=makeQuery(id+"F0.imprint","IMPRINT",FACE,{"disambiguationData":[TD([[makeQuery(id+"F0.imprint","IMPRINT",EDGE,{"disambiguationData":[TD([[subQ2,1.0]])],"derivedFrom":subQ1}),-1.0]])]});}
            var Q62;
            {var subQ0=sQuery(id+"F0.wireOp",EDGE,"E4.1.24.0");var subQ1=sQuery(id+"F0.wireOp",EDGE,"E0");var subQ2=makeQuery(id+"F0.imprint","INTERSECT",VERTEX,{"derivedFrom":[subQ1,subQ0]});Q62=makeQuery(id+"F0.imprint","IMPRINT",FACE,{"disambiguationData":[TD([[makeQuery(id+"F0.imprint","IMPRINT",EDGE,{"disambiguationData":[TD([[subQ2,1.0]])],"derivedFrom":subQ1}),-1.0]])]});}
            var Q63;
            {var subQ0=sQuery(id+"F0.wireOp",EDGE,"E4.1.16.0");var subQ1=sQuery(id+"F0.wireOp",EDGE,"E0");var subQ2=makeQuery(id+"F0.imprint","INTERSECT",VERTEX,{"derivedFrom":[subQ1,subQ0]});Q63=makeQuery(id+"F0.imprint","IMPRINT",FACE,{"disambiguationData":[TD([[makeQuery(id+"F0.imprint","IMPRINT",EDGE,{"disambiguationData":[TD([[subQ2,1.0]])],"derivedFrom":subQ1}),-1.0]])]});}
            var Q64;
            {var subQ0=sQuery(id+"F0.wireOp",EDGE,"E4.1.9.0");var subQ1=sQuery(id+"F0.wireOp",EDGE,"E0");var subQ2=makeQuery(id+"F0.imprint","INTERSECT",VERTEX,{"derivedFrom":[subQ1,subQ0]});Q64=makeQuery(id+"F0.imprint","IMPRINT",FACE,{"disambiguationData":[TD([[makeQuery(id+"F0.imprint","IMPRINT",EDGE,{"disambiguationData":[TD([[subQ2,1.0]])],"derivedFrom":subQ1}),-1.0]])]});}
            var Q65;
            {var subQ0=sQuery(id+"F0.wireOp",EDGE,"E4.1.21.0");var subQ1=sQuery(id+"F0.wireOp",EDGE,"E0");var subQ2=makeQuery(id+"F0.imprint","INTERSECT",VERTEX,{"derivedFrom":[subQ1,subQ0]});Q65=makeQuery(id+"F0.imprint","IMPRINT",FACE,{"disambiguationData":[TD([[makeQuery(id+"F0.imprint","IMPRINT",EDGE,{"disambiguationData":[TD([[subQ2,1.0]])],"derivedFrom":subQ1}),-1.0]])]});}
            var Q66;
            {var subQ0=sQuery(id+"F0.wireOp",EDGE,"E4.1.17.0");var subQ1=sQuery(id+"F0.wireOp",EDGE,"E0");var subQ2=makeQuery(id+"F0.imprint","INTERSECT",VERTEX,{"derivedFrom":[subQ1,subQ0]});Q66=makeQuery(id+"F0.imprint","IMPRINT",FACE,{"disambiguationData":[TD([[makeQuery(id+"F0.imprint","IMPRINT",EDGE,{"disambiguationData":[TD([[subQ2,1.0]])],"derivedFrom":subQ1}),-1.0]])]});}
            var Q67;
            {var subQ0=sQuery(id+"F0.wireOp",EDGE,"E4.1.25.0");var subQ1=sQuery(id+"F0.wireOp",EDGE,"E0");var subQ2=makeQuery(id+"F0.imprint","INTERSECT",VERTEX,{"derivedFrom":[subQ1,subQ0]});Q67=makeQuery(id+"F0.imprint","IMPRINT",FACE,{"disambiguationData":[TD([[makeQuery(id+"F0.imprint","IMPRINT",EDGE,{"disambiguationData":[TD([[subQ2,1.0]])],"derivedFrom":subQ1}),-1.0]])]});}
            var Q68;
            {var subQ0=sQuery(id+"F0.wireOp",EDGE,"E3.1.0");var subQ1=sQuery(id+"F0.wireOp",EDGE,"E0");var subQ2=makeQuery(id+"F0.imprint","INTERSECT",VERTEX,{"derivedFrom":[subQ1,subQ0]});Q68=makeQuery(id+"F0.imprint","IMPRINT",FACE,{"disambiguationData":[TD([[makeQuery(id+"F0.imprint","IMPRINT",EDGE,{"disambiguationData":[TD([[subQ2,1.0]])],"derivedFrom":subQ1}),-1.0]])]});}
            var Q69;
            {var subQ0=sQuery(id+"F0.wireOp",EDGE,"E4.1.8.0");var subQ1=sQuery(id+"F0.wireOp",EDGE,"E0");var subQ2=makeQuery(id+"F0.imprint","INTERSECT",VERTEX,{"derivedFrom":[subQ1,subQ0]});Q69=makeQuery(id+"F0.imprint","IMPRINT",FACE,{"disambiguationData":[TD([[makeQuery(id+"F0.imprint","IMPRINT",EDGE,{"disambiguationData":[TD([[subQ2,1.0]])],"derivedFrom":subQ1}),-1.0]])]});}
            var Q70;
            {var subQ0=sQuery(id+"F0.wireOp",EDGE,"E2");var subQ1=sQuery(id+"F0.wireOp",EDGE,"E0");var subQ2=makeQuery(id+"F0.imprint","INTERSECT",VERTEX,{"derivedFrom":[subQ1,subQ0]});Q70=makeQuery(id+"F0.imprint","IMPRINT",FACE,{"disambiguationData":[TD([[makeQuery(id+"F0.imprint","IMPRINT",EDGE,{"disambiguationData":[TD([[subQ2,-1.0]])],"derivedFrom":subQ1}),-1.0]])]});}
            extrude(context, id + "F1", {"entities" : qUnion([Q0, Q1, Q2, Q3, Q4, Q5, Q6, Q7, Q8, Q9, Q10, Q11, Q12, Q13, Q14, Q15, Q16, Q17, Q18, Q19, Q20, Q21, Q22, Q23, Q24, Q25, Q26, Q27, Q28, Q29, Q30, Q31, Q32, Q33, Q34, Q35, Q36, Q37, Q38, Q39, Q40, Q41, Q42, Q43, Q44, Q45, Q46, Q47, Q48, Q49, Q50, Q51, Q52, Q53, Q54, Q55, Q56, Q57, Q58, Q59, Q60, Q61, Q62, Q63, Q64, Q65, Q66, Q67, Q68, Q69, Q70]), "depth" : 25.4 * mm});
        }
        {
            var Q0;
            Q0=makeQuery(id+"F1.opExtrude","CAP_FACE",FACE,{"disambiguationData":[OSD([sQuery(id+"F0.wireOp",EDGE,"E1"),sQuery(id+"F0.wireOp",EDGE,"E2"),sQuery(id+"F0.wireOp",EDGE,"E3.1.0"),sQuery(id+"F0.wireOp",EDGE,"E3.1.1"),sQuery(id+"F0.wireOp",EDGE,"E3.2.0"),sQuery(id+"F0.wireOp",EDGE,"E3.2.1"),sQuery(id+"F0.wireOp",EDGE,"E4.1.3.0"),sQuery(id+"F0.wireOp",EDGE,"E4.3.3.0"),sQuery(id+"F0.wireOp",EDGE,"E4.1.4.0"),sQuery(id+"F0.wireOp",EDGE,"E4.3.4.0"),sQuery(id+"F0.wireOp",EDGE,"E4.1.5.0"),sQuery(id+"F0.wireOp",EDGE,"E4.3.5.0"),sQuery(id+"F0.wireOp",EDGE,"E4.1.6.0"),sQuery(id+"F0.wireOp",EDGE,"E4.3.6.0"),sQuery(id+"F0.wireOp",EDGE,"E4.1.7.0"),sQuery(id+"F0.wireOp",EDGE,"E4.3.7.0"),sQuery(id+"F0.wireOp",EDGE,"E4.1.8.0"),sQuery(id+"F0.wireOp",EDGE,"E4.3.8.0"),sQuery(id+"F0.wireOp",EDGE,"E4.1.9.0"),sQuery(id+"F0.wireOp",EDGE,"E4.3.9.0"),sQuery(id+"F0.wireOp",EDGE,"E4.1.10.0"),sQuery(id+"F0.wireOp",EDGE,"E4.3.10.0"),sQuery(id+"F0.wireOp",EDGE,"E4.1.11.0"),sQuery(id+"F0.wireOp",EDGE,"E4.3.11.0"),sQuery(id+"F0.wireOp",EDGE,"E4.1.12.0"),sQuery(id+"F0.wireOp",EDGE,"E4.3.12.0"),sQuery(id+"F0.wireOp",EDGE,"E4.1.13.0"),sQuery(id+"F0.wireOp",EDGE,"E4.3.13.0"),sQuery(id+"F0.wireOp",EDGE,"E4.1.14.0"),sQuery(id+"F0.wireOp",EDGE,"E4.3.14.0"),sQuery(id+"F0.wireOp",EDGE,"E4.1.15.0"),sQuery(id+"F0.wireOp",EDGE,"E4.3.15.0"),sQuery(id+"F0.wireOp",EDGE,"E4.1.16.0"),sQuery(id+"F0.wireOp",EDGE,"E4.3.16.0"),sQuery(id+"F0.wireOp",EDGE,"E4.1.17.0"),sQuery(id+"F0.wireOp",EDGE,"E4.3.17.0"),sQuery(id+"F0.wireOp",EDGE,"E4.1.18.0"),sQuery(id+"F0.wireOp",EDGE,"E4.3.18.0"),sQuery(id+"F0.wireOp",EDGE,"E4.1.19.0"),sQuery(id+"F0.wireOp",EDGE,"E4.3.19.0"),sQuery(id+"F0.wireOp",EDGE,"E4.1.20.0"),sQuery(id+"F0.wireOp",EDGE,"E4.3.20.0"),sQuery(id+"F0.wireOp",EDGE,"E4.1.21.0"),sQuery(id+"F0.wireOp",EDGE,"E4.3.21.0"),sQuery(id+"F0.wireOp",EDGE,"E4.1.22.0"),sQuery(id+"F0.wireOp",EDGE,"E4.3.22.0"),sQuery(id+"F0.wireOp",EDGE,"E4.1.23.0"),sQuery(id+"F0.wireOp",EDGE,"E4.3.23.0"),sQuery(id+"F0.wireOp",EDGE,"E4.1.24.0"),sQuery(id+"F0.wireOp",EDGE,"E4.3.24.0"),sQuery(id+"F0.wireOp",EDGE,"E4.1.25.0"),sQuery(id+"F0.wireOp",EDGE,"E4.3.25.0"),sQuery(id+"F0.wireOp",EDGE,"E4.1.26.0"),sQuery(id+"F0.wireOp",EDGE,"E4.3.26.0"),sQuery(id+"F0.wireOp",EDGE,"E4.1.27.0"),sQuery(id+"F0.wireOp",EDGE,"E4.3.27.0"),sQuery(id+"F0.wireOp",EDGE,"E4.1.28.0"),sQuery(id+"F0.wireOp",EDGE,"E4.3.28.0"),sQuery(id+"F0.wireOp",EDGE,"E4.1.29.0"),sQuery(id+"F0.wireOp",EDGE,"E4.3.29.0"),sQuery(id+"F0.wireOp",EDGE,"E4.1.30.0"),sQuery(id+"F0.wireOp",EDGE,"E4.3.30.0"),sQuery(id+"F0.wireOp",EDGE,"E4.1.31.0"),sQuery(id+"F0.wireOp",EDGE,"E4.3.31.0"),sQuery(id+"F0.wireOp",EDGE,"E4.1.32.0"),sQuery(id+"F0.wireOp",EDGE,"E4.3.32.0"),sQuery(id+"F0.wireOp",EDGE,"E4.1.33.0"),sQuery(id+"F0.wireOp",EDGE,"E4.3.33.0"),sQuery(id+"F0.wireOp",EDGE,"E4.1.34.0"),sQuery(id+"F0.wireOp",EDGE,"E4.3.34.0")])],"isStart":true});
            var sketch = newSketch(context, id + "F2", { "sketchPlane" : qUnion([Q0])});
            skCircle(sketch, "E5", {"center": v(0, 0) * mm, "radius": 2.54 * mm});
            skSolve(sketch);
        }
        {
            var Q0;
            Q0=makeQuery(id+"F2.imprint","IMPRINT",FACE,{"disambiguationData":[TD([[makeQuery(id+"F2.imprint","IMPRINT",EDGE,{"derivedFrom":sQuery(id+"F2.wireOp",EDGE,"E5")}),1.0]])]});
            extrude(context, id + "F3", {"entities" : qUnion([Q0]), "operationType" : NewBodyOperationType.REMOVE, "oppositeDirection" : true, "depth" : 10.16 * mm});
        }
    });
